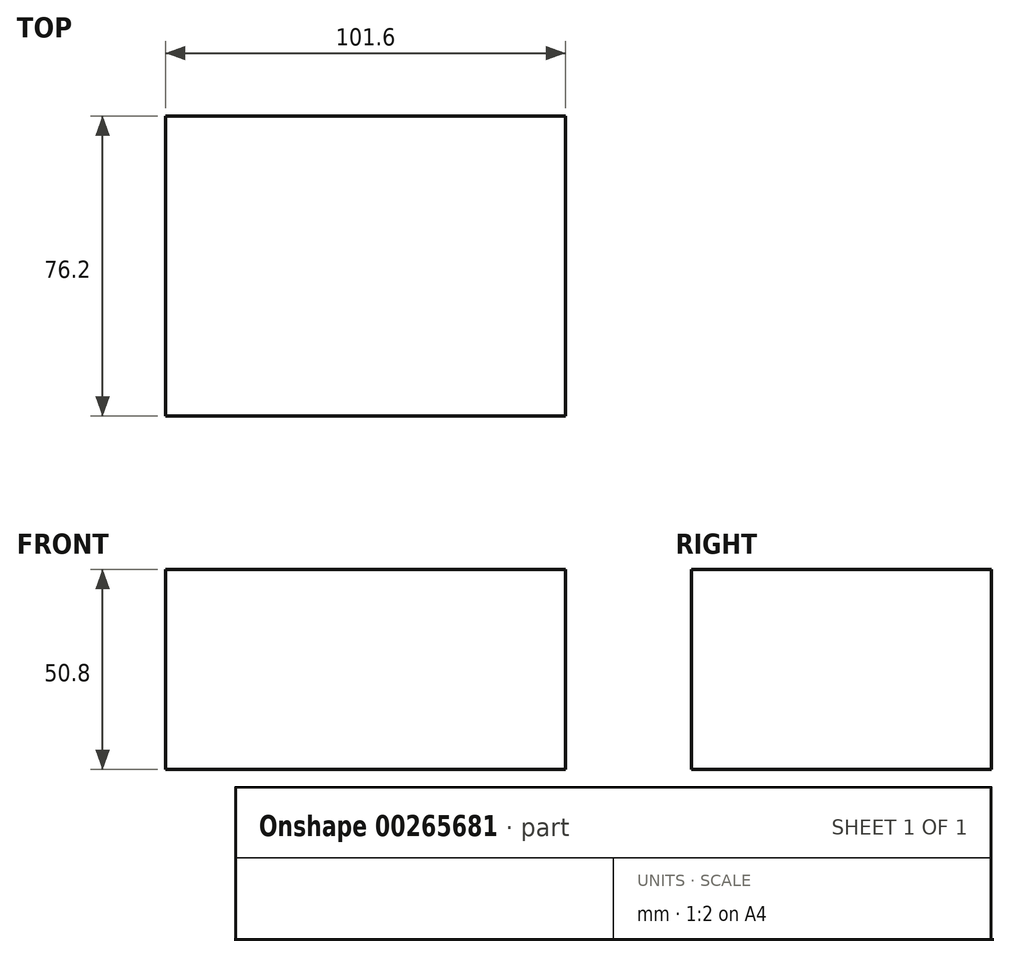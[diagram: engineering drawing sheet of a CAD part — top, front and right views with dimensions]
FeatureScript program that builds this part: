
annotation { "Feature Type Name" : "Feature", "Feature Type Description" : "" }
export const myFeature = defineFeature(function(context is Context, id is Id, definition is map)
    precondition{}
    {
        {
            var Q0;
            Q0=qCreatedBy(makeId("Front.planeOp"),FACE);
            var sketch = newSketch(context, id + "F0", { "sketchPlane" : qUnion([Q0])});
            skLineSegment(sketch, "E0.bottom", {"start": v(-59.74, 18.9) * mm, "end": v(41.86, 18.9) * mm});
            skLineSegment(sketch, "E0.top", {"start": v(-59.74, -31.9) * mm, "end": v(41.86, -31.9) * mm});
            skLineSegment(sketch, "E0.left", {"start": v(-59.74, 18.9) * mm, "end": v(-59.74, -31.9) * mm});
            skLineSegment(sketch, "E0.right", {"start": v(41.86, 18.9) * mm, "end": v(41.86, -31.9) * mm});
            skSolve(sketch);
        }
        {
            var Q0;
            Q0 = qSketchRegion(id + "F0", true);
            extrude(context, id + "F1", {"entities" : qUnion([Q0]), "depth" : 76.2 * mm});
        }
    });
